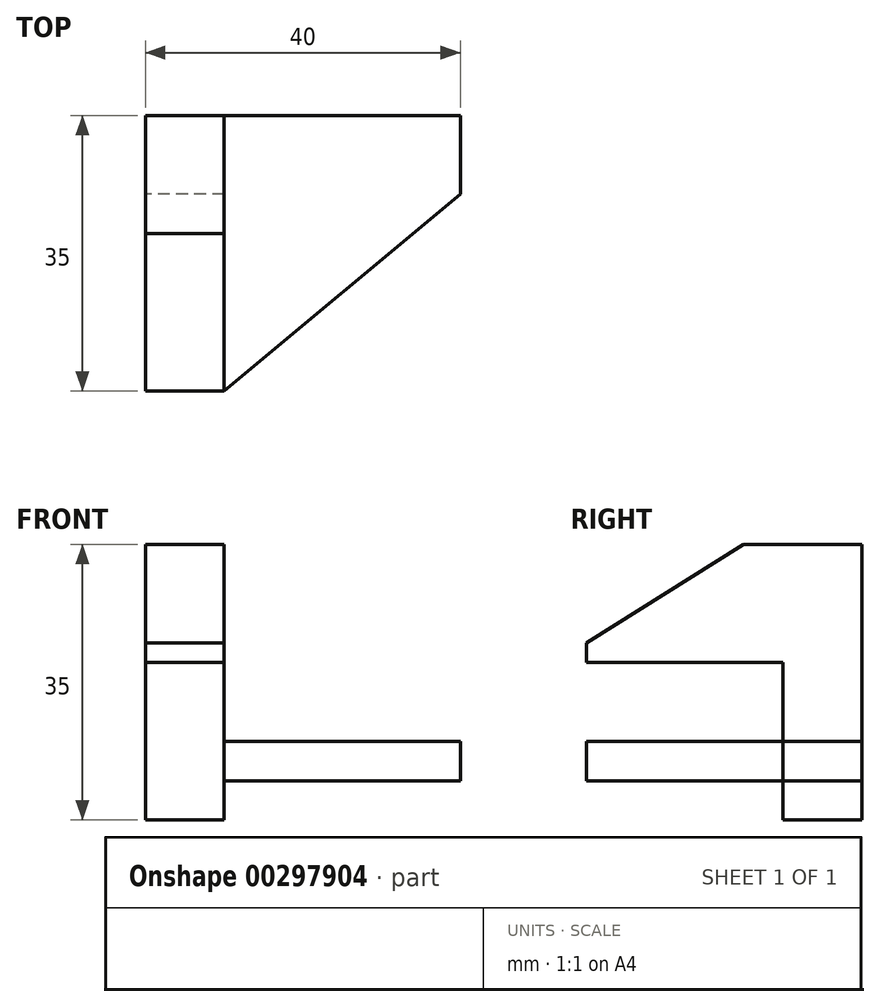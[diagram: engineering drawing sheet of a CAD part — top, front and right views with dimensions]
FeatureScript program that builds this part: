
annotation { "Feature Type Name" : "Feature", "Feature Type Description" : "" }
export const myFeature = defineFeature(function(context is Context, id is Id, definition is map)
    precondition{}
    {
        {
            var Q0;
            Q0=qCreatedBy(makeId("Front.planeOp"),FACE);
            var sketch = newSketch(context, id + "F0", { "sketchPlane" : qUnion([Q0])});
            skLineSegment(sketch, "E0.bottom", {"start": v(32.5, 20) * mm, "end": v(-32.5, 20) * mm});
            skLineSegment(sketch, "E0.top", {"start": v(32.5, -20) * mm, "end": v(-32.5, -20) * mm});
            skLineSegment(sketch, "E0.left", {"start": v(32.5, 20) * mm, "end": v(32.5, -20) * mm});
            skLineSegment(sketch, "E0.right", {"start": v(-32.5, 20) * mm, "end": v(-32.5, -20) * mm});
            skPoint(sketch, "E0.middle", {"position": v(0, 0) * mm});
            skLineSegment(sketch, "E1.bottom", {"start": v(-32.5, -20) * mm, "end": v(-22.5, -20) * mm});
            skLineSegment(sketch, "E1.top", {"start": v(-32.5, 0) * mm, "end": v(-22.5, 0) * mm});
            skLineSegment(sketch, "E1.left", {"start": v(-32.5, -20) * mm, "end": v(-32.5, 0) * mm});
            skLineSegment(sketch, "E1.right", {"start": v(-22.5, -20) * mm, "end": v(-22.5, 0) * mm});
            skLineSegment(sketch, "E2.top", {"start": v(-32.5, 15) * mm, "end": v(-22.5, 15) * mm});
            skLineSegment(sketch, "E2.left", {"start": v(-32.5, 0) * mm, "end": v(-32.5, 15) * mm});
            skLineSegment(sketch, "E2.right", {"start": v(-22.5, 0) * mm, "end": v(-22.5, 15) * mm});
            skLineSegment(sketch, "E3.bottom", {"start": v(-22.5, -15) * mm, "end": v(7.5, -15) * mm});
            skLineSegment(sketch, "E3.top", {"start": v(-22.5, -10) * mm, "end": v(7.5, -10) * mm});
            skLineSegment(sketch, "E3.left", {"start": v(-22.5, -15) * mm, "end": v(-22.5, -10) * mm});
            skLineSegment(sketch, "E3.right", {"start": v(7.5, -15) * mm, "end": v(7.5, -10) * mm});
            skCircle(sketch, "E4", {"center": v(17.5, -7.16) * mm, "radius": 5 * mm});
            skLineSegment(sketch, "E5", {"start": v(-7.5, 20) * mm, "end": v(32.5, 0) * mm});
            skSolve(sketch);
        }
        {
            var Q0;
            {var subQ3=sQuery(id+"F0.wireOp",EDGE,"E1.bottom");Q0=makeQuery(id+"F0.imprint","IMPRINT",FACE,{"disambiguationData":[TD([[makeQuery(id+"F0.imprint","IMPRINT",EDGE,{"derivedFrom":subQ3}),1.0]])]});}
            var Q1;
            Q1=makeQuery(id+"F0.imprint","IMPRINT",FACE,{"disambiguationData":[TD([[makeQuery(id+"F0.imprint","IMPRINT",EDGE,{"derivedFrom":sQuery(id+"F0.wireOp",EDGE,"E3.bottom")}),1.0]])]});
            extrude(context, id + "F1", {"entities" : qUnion([Q0, Q1]), "depth" : 35 * mm});
        }
        {
            var Q0;
            {var subQ5=sQuery(id+"F0.wireOp",EDGE,"E0.top");Q0=makeQuery(id+"F0.imprint","IMPRINT",FACE,{"disambiguationData":[TD([[makeQuery(id+"F0.imprint","IMPRINT",EDGE,{"derivedFrom":subQ5}),-1.0]])]});}
            extrude(context, id + "F2", {"entities" : qUnion([Q0]), "operationType" : NewBodyOperationType.ADD, "depth" : 10 * mm});
        }
        {
            var Q0;
            Q0=makeQuery(id+"F0.imprint","IMPRINT",FACE,{"disambiguationData":[TD([[makeQuery(id+"F0.imprint","IMPRINT",EDGE,{"derivedFrom":sQuery(id+"F0.wireOp",EDGE,"E1.top")}),1.0]])]});
            extrude(context, id + "F3", {"entities" : qUnion([Q0]), "operationType" : NewBodyOperationType.ADD, "depth" : 35 * mm});
        }
        {
            var Q0;
            Q0=makeQuery(id+"F1.opExtrude","SWEPT_FACE",FACE,{"disambiguationData":[OSD([sQuery(id+"F0.wireOp",EDGE,"E3.top")])]});
            var sketch = newSketch(context, id + "F4", { "sketchPlane" : qUnion([Q0])});
            skLineSegment(sketch, "E6", {"start": v(-22.5, -35) * mm, "end": v(7.5, -10) * mm});
            skSolve(sketch);
        }
        {
            var Q0;
            Q0=makeQuery(id+"F4.imprint","IMPRINT",FACE,{"disambiguationData":[TD([[makeQuery(id+"F4.imprint","IMPRINT",EDGE,{"derivedFrom":sQuery(id+"F4.wireOp",EDGE,"E6")}),-1.0]])]});
            extrude(context, id + "F5", {"entities" : qUnion([Q0]), "operationType" : NewBodyOperationType.REMOVE, "endBound" : BoundingType.THROUGH_ALL, "oppositeDirection" : true, "depth" : 25 * mm});
        }
        {
            var Q0;
            {var subQ0=sQuery(id+"F0.wireOp",EDGE,"E2.right");var subQ1=sQuery(id+"F0.wireOp",EDGE,"E1.right");Q0=makeQuery(id+"F3.boolean.opBoolean","MERGE",FACE,{"derivedFrom":[makeQuery(id+"F1.opExtrude","SWEPT_FACE",FACE,{"disambiguationData":[OSD([subQ1]),TDD([makeQuery(id+"F0.imprint","IMPRINT",EDGE,{"disambiguationData":[TD([[makeQuery(id+"F0.imprint","INTERSECT",VERTEX,{"derivedFrom":[subQ1,sQuery(id+"F0.wireOp",EDGE,"E1.top"),subQ0]}),1.0]])],"derivedFrom":subQ1})])]}),makeQuery(id+"F3.opExtrude","SWEPT_FACE",FACE,{"disambiguationData":[OSD([subQ0])]})]});}
            var sketch = newSketch(context, id + "F6", { "sketchPlane" : qUnion([Q0])});
            skLineSegment(sketch, "E7", {"start": v(-35, 2.5) * mm, "end": v(-15, 15) * mm});
            skSolve(sketch);
        }
        {
            var Q0;
            {var subQ0=sQuery(id+"F6.wireOp",EDGE,"E7");Q0=makeQuery(id+"F6.imprint","IMPRINT",FACE,{"disambiguationData":[TD([[makeQuery(id+"F6.imprint","IMPRINT",EDGE,{"derivedFrom":subQ0}),1.0]])]});}
            extrude(context, id + "F7", {"entities" : qUnion([Q0]), "operationType" : NewBodyOperationType.REMOVE, "endBound" : BoundingType.THROUGH_ALL, "oppositeDirection" : true, "depth" : 25 * mm});
        }
    });
